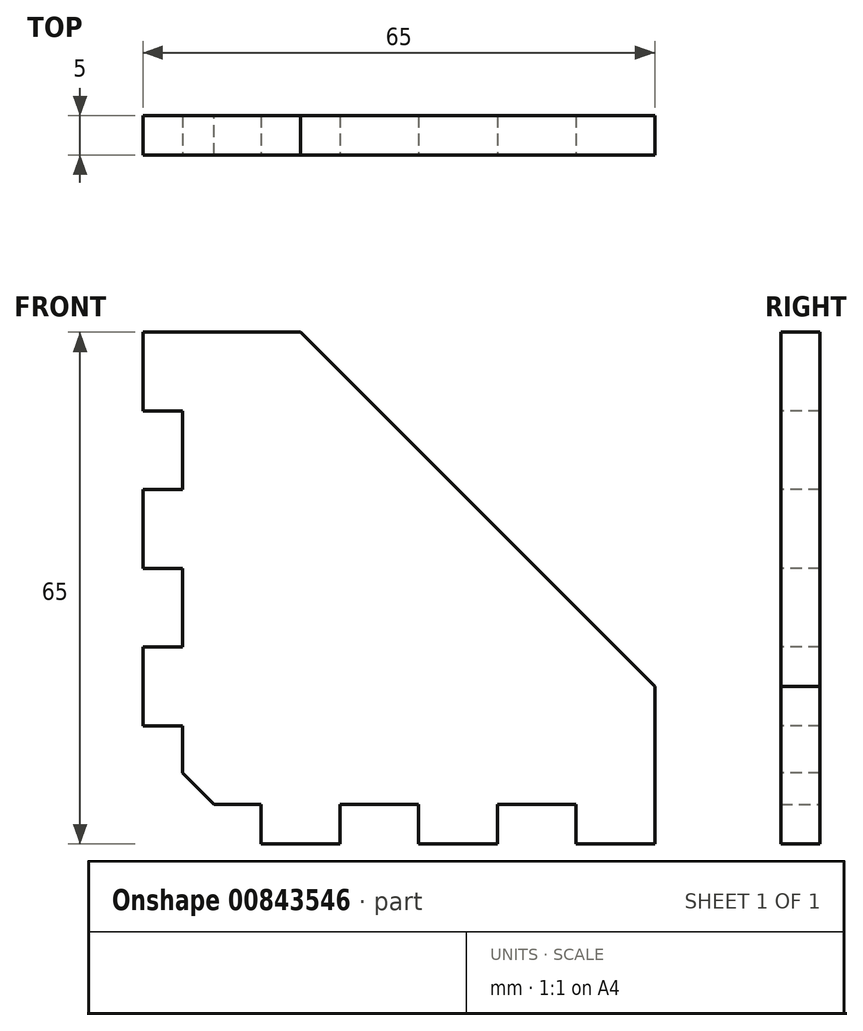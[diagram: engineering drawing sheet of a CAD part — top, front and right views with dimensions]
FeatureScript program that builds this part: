
annotation { "Feature Type Name" : "Feature", "Feature Type Description" : "" }
export const myFeature = defineFeature(function(context is Context, id is Id, definition is map)
    precondition{}
    {
        {
            var Q0;
            Q0=qCreatedBy(makeId("Front.planeOp"),FACE);
            var sketch = newSketch(context, id + "F0", { "sketchPlane" : qUnion([Q0])});
            skLineSegment(sketch, "E0.bottom", {"start": v(30, 30) * mm, "end": v(-30, 30) * mm, "construction": true});
            skLineSegment(sketch, "E0.top", {"start": v(30, -30) * mm, "end": v(-30, -30) * mm});
            skLineSegment(sketch, "E0.left", {"start": v(30, 30) * mm, "end": v(30, -30) * mm, "construction": true});
            skLineSegment(sketch, "E0.right", {"start": v(-30, 30) * mm, "end": v(-30, -30) * mm});
            skPoint(sketch, "E0.middle", {"position": v(0, 0) * mm});
            skLineSegment(sketch, "E1", {"start": v(-30, 30) * mm, "end": v(-15, 30) * mm});
            skLineSegment(sketch, "E2", {"start": v(-15, 30) * mm, "end": v(30, -15) * mm});
            skLineSegment(sketch, "E3", {"start": v(30, -15) * mm, "end": v(30, -30) * mm});
            skSolve(sketch);
        }
        {
            var Q0;
            Q0 = qSketchRegion(id + "F0", true);
            extrude(context, id + "F1", {"entities" : qUnion([Q0]), "endBound" : BoundingType.SYMMETRIC, "depth" : 5 * mm, "offsetDistance" : 25 * mm});
        }
        {
            var Q0;
            Q0=makeQuery(id+"F1.opExtrude","CAP_FACE",FACE,{"disambiguationData":[OSD([sQuery(id+"F0.wireOp",EDGE,"E0.top"),sQuery(id+"F0.wireOp",EDGE,"E0.right"),sQuery(id+"F0.wireOp",EDGE,"E1"),sQuery(id+"F0.wireOp",EDGE,"E2"),sQuery(id+"F0.wireOp",EDGE,"E3")])],"isStart":false});
            var sketch = newSketch(context, id + "F2", { "sketchPlane" : qUnion([Q0])});
            skLineSegment(sketch, "E4.bottom", {"start": v(-30, 30) * mm, "end": v(-35, 30) * mm});
            skLineSegment(sketch, "E4.top", {"start": v(-30, 20) * mm, "end": v(-35, 20) * mm});
            skLineSegment(sketch, "E4.left", {"start": v(-30, 30) * mm, "end": v(-30, 20) * mm});
            skLineSegment(sketch, "E4.right", {"start": v(-35, 30) * mm, "end": v(-35, 20) * mm});
            skLineSegment(sketch, "E5.0.1.0", {"start": v(-30, 0) * mm, "end": v(-35, 0) * mm});
            skLineSegment(sketch, "E5.0.1.1", {"start": v(-30, 10) * mm, "end": v(-35, 10) * mm});
            skLineSegment(sketch, "E5.0.1.2", {"start": v(-30, 10) * mm, "end": v(-30, 0) * mm});
            skLineSegment(sketch, "E5.0.1.3", {"start": v(-35, 10) * mm, "end": v(-35, 0) * mm});
            skLineSegment(sketch, "E5.0.2.0", {"start": v(-30, -20) * mm, "end": v(-35, -20) * mm});
            skLineSegment(sketch, "E5.0.2.1", {"start": v(-30, -10) * mm, "end": v(-35, -10) * mm});
            skLineSegment(sketch, "E5.0.2.2", {"start": v(-30, -10) * mm, "end": v(-30, -20) * mm});
            skLineSegment(sketch, "E5.0.2.3", {"start": v(-35, -10) * mm, "end": v(-35, -20) * mm});
            skLineSegment(sketch, "E5.direction1", {"start": v(-35, 20) * mm, "end": v(-10, 20) * mm, "construction": true});
            skLineSegment(sketch, "E5.direction2", {"start": v(-35, 20) * mm, "end": v(-35, 0) * mm, "construction": true});
            skLineSegment(sketch, "E6.bottom", {"start": v(30, -30) * mm, "end": v(20, -30) * mm});
            skLineSegment(sketch, "E6.top", {"start": v(30, -35) * mm, "end": v(20, -35) * mm});
            skLineSegment(sketch, "E6.left", {"start": v(30, -30) * mm, "end": v(30, -35) * mm});
            skLineSegment(sketch, "E6.right", {"start": v(20, -30) * mm, "end": v(20, -35) * mm});
            skLineSegment(sketch, "E7.1.0.0", {"start": v(10, -35) * mm, "end": v(0, -35) * mm});
            skLineSegment(sketch, "E7.1.0.1", {"start": v(0, -30) * mm, "end": v(0, -35) * mm});
            skLineSegment(sketch, "E7.1.0.2", {"start": v(10, -30) * mm, "end": v(0, -30) * mm});
            skLineSegment(sketch, "E7.1.0.3", {"start": v(10, -30) * mm, "end": v(10, -35) * mm});
            skLineSegment(sketch, "E7.2.0.0", {"start": v(-10, -35) * mm, "end": v(-20, -35) * mm});
            skLineSegment(sketch, "E7.2.0.1", {"start": v(-20, -30) * mm, "end": v(-20, -35) * mm});
            skLineSegment(sketch, "E7.2.0.2", {"start": v(-10, -30) * mm, "end": v(-20, -30) * mm});
            skLineSegment(sketch, "E7.2.0.3", {"start": v(-10, -30) * mm, "end": v(-10, -35) * mm});
            skLineSegment(sketch, "E7.direction1", {"start": v(20, -35) * mm, "end": v(0, -35) * mm, "construction": true});
            skSolve(sketch);
        }
        {
            var Q0;
            Q0 = qSketchRegion(id + "F2", true);
            var Q1;
            Q1=makeQuery(id+"F1.opExtrude","CAP_FACE",FACE,{"disambiguationData":[OSD([sQuery(id+"F0.wireOp",EDGE,"E0.top"),sQuery(id+"F0.wireOp",EDGE,"E0.right"),sQuery(id+"F0.wireOp",EDGE,"E1"),sQuery(id+"F0.wireOp",EDGE,"E2"),sQuery(id+"F0.wireOp",EDGE,"E3")])],"isStart":true});
            extrude(context, id + "F3", {"entities" : qUnion([Q0]), "operationType" : NewBodyOperationType.ADD, "endBound" : BoundingType.UP_TO_SURFACE, "oppositeDirection" : true, "depth" : 25 * mm, "endBoundEntityFace" : qUnion([Q1]), "offsetDistance" : 25 * mm});
        }
        {
            var Q0;
            Q0=makeQuery(id+"F1.opExtrude","SWEPT_EDGE",EDGE,{"disambiguationData":[OSD([sQuery(id+"F0.wireOp",EDGE,"E0.top"),sQuery(id+"F0.wireOp",EDGE,"E0.right")])]});
            chamfer(context, id + "F4", {"entities" : qUnion([Q0]), "width" : 4 * mm, "tangentPropagation" : true});
        }
    });
